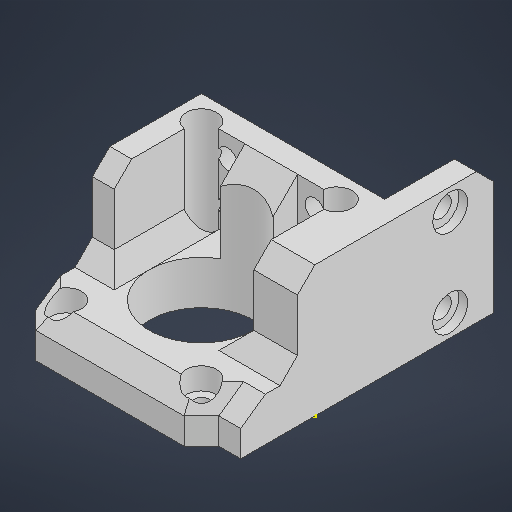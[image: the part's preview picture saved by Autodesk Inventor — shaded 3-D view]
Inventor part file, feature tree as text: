
AUTODESK INVENTOR PART (.ipt)
format: ipt  version: 2025.1 (Build 291241000, 241)  size: 555,008 bytes
history: native  units: mm
features: extrude x7, sketch x6, chamfer x5, projected_geometry x3, plane x1, hole x1
ambient origin geometry x8: Origin, YZ Plane, XZ Plane, XY Plane, X Axis, Y Axis, Z Axis, Center Point
bodies: Solid1 (feature_tree)
feature tree (23):
  sketch  "Sketch1"  dims[d0=42.0mm d1=42.0mm]
  extrude  "Extrusion1"  Depth=42.0mm
  extrude  "Extrusion3"  Depth=3.4mm
  sketch  "Sketch4"  dims[d4=7.0mm d5=10.0mm d6=0.0mm]
  plane  "Work Plane1"
  extrude  "Extrusion4"  Depth=10.0mm TaperAngle=0.0deg
  extrude  "Extrusion5"  Depth=20.0mm TaperAngle=0.0deg
  extrude  "Extrusion6"  Depth=20.0mm
  chamfer  "Chamfer4"  [1 undecoded]
  chamfer  "Chamfer5"  Distance=30.0mm
  extrude  "Extrusion7"  TaperAngle=0.0deg  [1 undecoded]
  chamfer  "Chamfer7"  [1 undecoded]
  chamfer  "Chamfer8"  Distance=31.0mm
  extrude  "Extrusion8"  Depth=4.0mm TaperAngle=45.0deg
  chamfer  "Chamfer10"  Distance=20.0mm Angle=45.0deg
  hole  "Hole1"  [1 undecoded]
  sketch  "Sketch7"  dims[d14=15.0mm d21=-5.0mm d28=30.0mm d29=0.0mm d30=0.0mm d31=0.0mm d32=0.0mm d33=0.0mm d37=31.0mm d38=4.0mm d39=2.0mm d40=45.0deg d41=20.0mm d42=2.0mm d43=45.0deg d44=6.0mm d45=12.071797mm d46=6.0mm d48=20.0mm d49=4.5mm d50=10.0mm d51=0.0mm d52=0.0mm d58=5.0mm d59=20.0mm d60=20.0mm d61=4.0mm d62=20.0mm d63=45.0deg d64=4.0mm d65=20.0mm d66=45.0deg d70=20.0mm d72=5.0mm d74=5.0mm d75=0.0mm d76=4.0mm d77=20.0mm d78=45.0deg d79=4.5mm d80=6.0mm d81=8.0mm d82=2.0mm d83=90.0deg d84=8.0mm d85=20.594885mm d15=0.872665mm d55=0.0mm d56=0.0mm d57=0.0mm]
  sketch  "Sketch3"  dims[d2=24.0mm d3=3.4mm]
  projected_geometry  "Projected Loop1"
  projected_geometry  "Projected Loop2"
  sketch  "Sketch5"  dims[d9=5.0mm d10=20.0mm d11=0.0mm]
  projected_geometry  "Projected Loop3"
  sketch  "Sketch6"  dims[d12=20.0mm d13=4.5mm]
note: 4 required parameter values undecoded (feature->parameter linkage not recoverable at this tier; creation-order binding heuristic only, values carry confidence <= 0.55)
